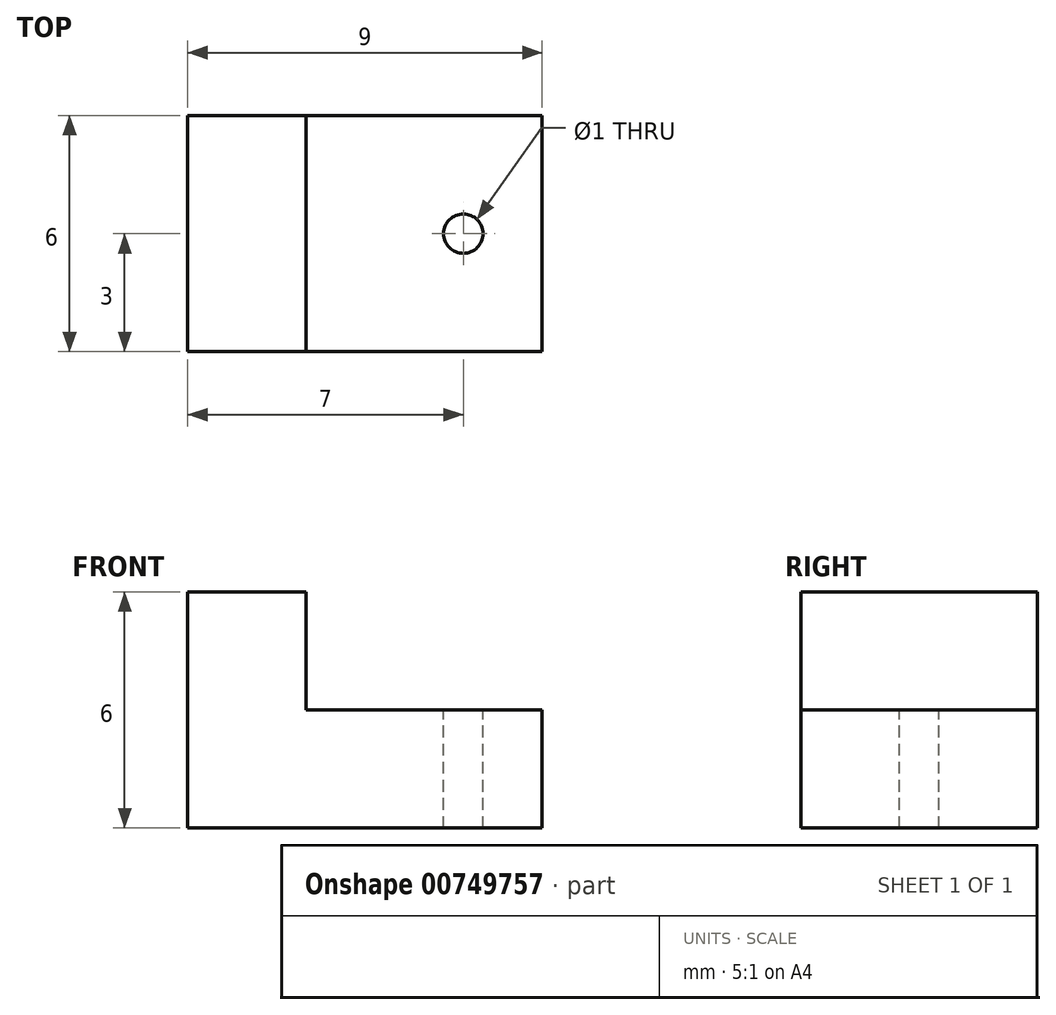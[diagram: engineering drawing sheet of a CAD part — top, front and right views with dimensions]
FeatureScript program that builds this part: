
annotation { "Feature Type Name" : "Feature", "Feature Type Description" : "" }
export const myFeature = defineFeature(function(context is Context, id is Id, definition is map)
    precondition{}
    {
        {
            var Q0;
            Q0=qCreatedBy(makeId("Front.planeOp"),FACE);
            var sketch = newSketch(context, id + "F0", { "sketchPlane" : qUnion([Q0])});
            skLineSegment(sketch, "E0.bottom", {"start": v(0, 0) * mm, "end": v(9, 0) * mm});
            skLineSegment(sketch, "E0.top", {"start": v(0, 6) * mm, "end": v(9, 6) * mm});
            skLineSegment(sketch, "E0.left", {"start": v(0, 0) * mm, "end": v(0, 6) * mm});
            skLineSegment(sketch, "E0.right", {"start": v(9, 0) * mm, "end": v(9, 6) * mm});
            skSolve(sketch);
        }
        {
            var Q0;
            Q0 = qSketchRegion(id + "F0", true);
            extrude(context, id + "F1", {"entities" : qUnion([Q0]), "depth" : 6 * mm, "offsetDistance" : 25 * mm});
        }
        {
            var Q0;
            Q0=makeQuery(id+"F1.opExtrude","CAP_FACE",FACE,{"disambiguationData":[OSD([sQuery(id+"F0.wireOp",EDGE,"E0.bottom"),sQuery(id+"F0.wireOp",EDGE,"E0.top"),sQuery(id+"F0.wireOp",EDGE,"E0.left"),sQuery(id+"F0.wireOp",EDGE,"E0.right")])],"isStart":false});
            var sketch = newSketch(context, id + "F2", { "sketchPlane" : qUnion([Q0])});
            skLineSegment(sketch, "E1.bottom", {"start": v(9, 6) * mm, "end": v(3, 6) * mm});
            skLineSegment(sketch, "E1.top", {"start": v(9, 3) * mm, "end": v(3, 3) * mm});
            skLineSegment(sketch, "E1.left", {"start": v(9, 6) * mm, "end": v(9, 3) * mm});
            skLineSegment(sketch, "E1.right", {"start": v(3, 6) * mm, "end": v(3, 3) * mm});
            skSolve(sketch);
        }
        {
            var Q0;
            Q0 = qSketchRegion(id + "F2", true);
            extrude(context, id + "F3", {"entities" : qUnion([Q0]), "operationType" : NewBodyOperationType.REMOVE, "endBound" : BoundingType.THROUGH_ALL, "oppositeDirection" : true, "depth" : 25 * mm, "offsetDistance" : 25 * mm});
        }
        {
            var Q0;
            Q0=makeQuery(id+"F3.boolean.opBoolean","COPY",FACE,{"derivedFrom":makeQuery(id+"F3.opExtrude","SWEPT_FACE",FACE,{"disambiguationData":[OSD([sQuery(id+"F2.wireOp",EDGE,"E1.top")])]})});
            var sketch = newSketch(context, id + "F4", { "sketchPlane" : qUnion([Q0])});
            skCircle(sketch, "E2", {"center": v(7, -3) * mm, "radius": 0.5 * mm});
            skSolve(sketch);
        }
        {
            var Q0;
            Q0=makeQuery(id+"F4.imprint","IMPRINT",FACE,{"disambiguationData":[TD([[makeQuery(id+"F4.imprint","IMPRINT",EDGE,{"derivedFrom":sQuery(id+"F4.wireOp",EDGE,"E2")}),1.0]])]});
            extrude(context, id + "F5", {"entities" : qUnion([Q0]), "operationType" : NewBodyOperationType.REMOVE, "endBound" : BoundingType.THROUGH_ALL, "oppositeDirection" : true, "depth" : 25 * mm, "offsetDistance" : 25 * mm});
        }
    });
